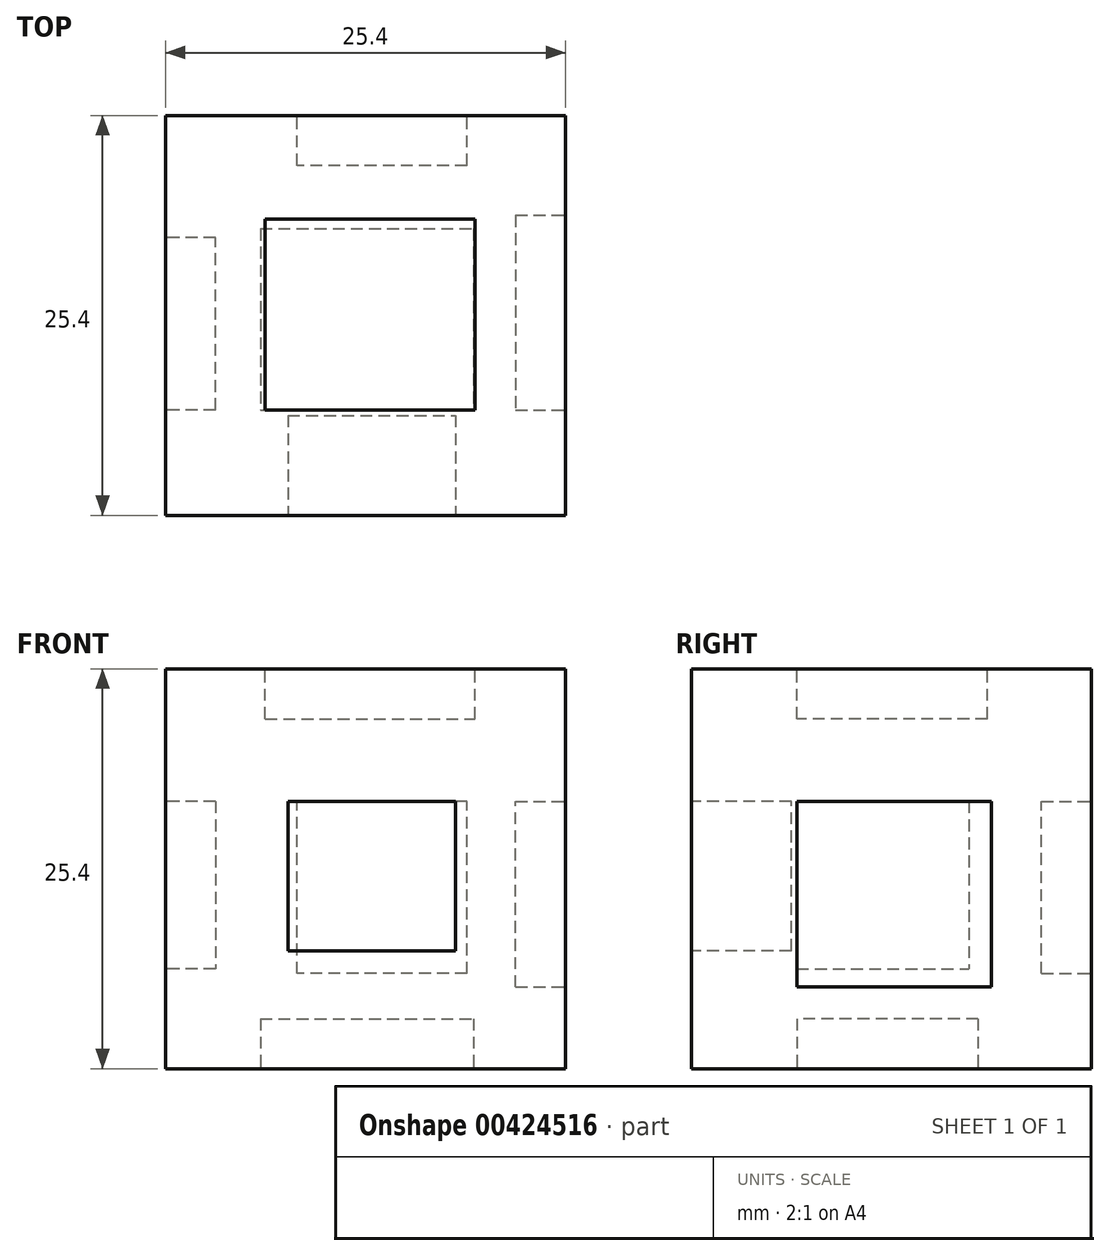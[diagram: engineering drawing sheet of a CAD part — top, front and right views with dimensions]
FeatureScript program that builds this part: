
annotation { "Feature Type Name" : "Feature", "Feature Type Description" : "" }
export const myFeature = defineFeature(function(context is Context, id is Id, definition is map)
    precondition{}
    {
        {
            var Q0;
            Q0=qCreatedBy(makeId("Right.planeOp"),FACE);
            var sketch = newSketch(context, id + "F0", { "sketchPlane" : qUnion([Q0])});
            skLineSegment(sketch, "E0.bottom", {"start": v(-6.7, 8.42) * mm, "end": v(18.7, 8.42) * mm});
            skLineSegment(sketch, "E0.top", {"start": v(-6.7, -16.98) * mm, "end": v(18.7, -16.98) * mm});
            skLineSegment(sketch, "E0.left", {"start": v(-6.7, 8.42) * mm, "end": v(-6.7, -16.98) * mm});
            skLineSegment(sketch, "E0.right", {"start": v(18.7, 8.42) * mm, "end": v(18.7, -16.98) * mm});
            skSolve(sketch);
        }
        {
            var Q0;
            Q0 = qSketchRegion(id + "F0", true);
            extrude(context, id + "F1", {"entities" : qUnion([Q0]), "depth" : 25.4 * mm});
        }
        {
            var Q0;
            Q0=makeQuery(id+"F1.opExtrude","SWEPT_FACE",FACE,{"disambiguationData":[OSD([sQuery(id+"F0.wireOp",EDGE,"E0.left")])]});
            var sketch = newSketch(context, id + "F2", { "sketchPlane" : qUnion([Q0])});
            skLineSegment(sketch, "E1.bottom", {"start": v(7.77, -9.5) * mm, "end": v(18.42, -9.5) * mm});
            skLineSegment(sketch, "E1.top", {"start": v(7.77, 0) * mm, "end": v(18.42, 0) * mm});
            skLineSegment(sketch, "E1.left", {"start": v(7.77, -9.5) * mm, "end": v(7.77, 0) * mm});
            skLineSegment(sketch, "E1.right", {"start": v(18.42, -9.5) * mm, "end": v(18.42, 0) * mm});
            skSolve(sketch);
        }
        {
            var Q0;
            Q0 = qSketchRegion(id + "F2", true);
            extrude(context, id + "F3", {"entities" : qUnion([Q0]), "oppositeDirection" : true, "depth" : 6.35 * mm});
        }
        {
            var Q0;
            Q0=makeQuery(id+"F1.opExtrude","CAP_FACE",FACE,{"disambiguationData":[OSD([sQuery(id+"F0.wireOp",EDGE,"E0.bottom"),sQuery(id+"F0.wireOp",EDGE,"E0.top"),sQuery(id+"F0.wireOp",EDGE,"E0.left"),sQuery(id+"F0.wireOp",EDGE,"E0.right")])],"isStart":true});
            var sketch = newSketch(context, id + "F4", { "sketchPlane" : qUnion([Q0])});
            skLineSegment(sketch, "E2.bottom", {"start": v(0, 0) * mm, "end": v(-10.94, 0) * mm});
            skLineSegment(sketch, "E2.top", {"start": v(0, -10.65) * mm, "end": v(-10.94, -10.65) * mm});
            skLineSegment(sketch, "E2.left", {"start": v(0, 0) * mm, "end": v(0, -10.65) * mm});
            skLineSegment(sketch, "E2.right", {"start": v(-10.94, 0) * mm, "end": v(-10.94, -10.65) * mm});
            skSolve(sketch);
        }
        {
            var Q0;
            Q0=makeQuery(id+"F1.opExtrude","CAP_FACE",FACE,{"disambiguationData":[OSD([sQuery(id+"F0.wireOp",EDGE,"E0.bottom"),sQuery(id+"F0.wireOp",EDGE,"E0.top"),sQuery(id+"F0.wireOp",EDGE,"E0.left"),sQuery(id+"F0.wireOp",EDGE,"E0.right")])],"isStart":false});
            var sketch = newSketch(context, id + "F5", { "sketchPlane" : qUnion([Q0])});
            skLineSegment(sketch, "E3.bottom", {"start": v(12.38, -11.8) * mm, "end": v(0, -11.8) * mm});
            skLineSegment(sketch, "E3.top", {"start": v(12.38, 0) * mm, "end": v(0, 0) * mm});
            skLineSegment(sketch, "E3.left", {"start": v(12.38, -11.8) * mm, "end": v(12.38, 0) * mm});
            skLineSegment(sketch, "E3.right", {"start": v(0, -11.8) * mm, "end": v(0, 0) * mm});
            skSolve(sketch);
        }
        {
            var Q0;
            Q0 = qSketchRegion(id + "F5", true);
            extrude(context, id + "F6", {"entities" : qUnion([Q0]), "oppositeDirection" : true, "depth" : 3.17 * mm});
        }
        {
            var Q0;
            Q0=makeQuery(id+"F1.opExtrude","SWEPT_FACE",FACE,{"disambiguationData":[OSD([sQuery(id+"F0.wireOp",EDGE,"E0.right")])]});
            var sketch = newSketch(context, id + "F7", { "sketchPlane" : qUnion([Q0])});
            skLineSegment(sketch, "E4.bottom", {"start": v(-19.15, -10.94) * mm, "end": v(-8.35, -10.94) * mm});
            skLineSegment(sketch, "E4.top", {"start": v(-19.15, 0) * mm, "end": v(-8.35, 0) * mm});
            skLineSegment(sketch, "E4.left", {"start": v(-19.15, -10.94) * mm, "end": v(-19.15, 0) * mm});
            skLineSegment(sketch, "E4.right", {"start": v(-8.35, -10.94) * mm, "end": v(-8.35, 0) * mm});
            skSolve(sketch);
        }
        {
            var Q0;
            Q0 = qSketchRegion(id + "F7", true);
            extrude(context, id + "F8", {"entities" : qUnion([Q0]), "oppositeDirection" : true, "depth" : 3.17 * mm});
        }
        {
            var Q0;
            Q0 = qSketchRegion(id + "F4", true);
            extrude(context, id + "F9", {"entities" : qUnion([Q0]), "oppositeDirection" : true, "depth" : 3.17 * mm});
        }
        {
            var Q0;
            Q0=makeQuery(id+"F1.opExtrude","SWEPT_FACE",FACE,{"disambiguationData":[OSD([sQuery(id+"F0.wireOp",EDGE,"E0.top")])]});
            var sketch = newSketch(context, id + "F10", { "sketchPlane" : qUnion([Q0])});
            skLineSegment(sketch, "E5.bottom", {"start": v(6.02, -11.51) * mm, "end": v(19.55, -11.51) * mm});
            skLineSegment(sketch, "E5.top", {"start": v(6.02, 0) * mm, "end": v(19.55, 0) * mm});
            skLineSegment(sketch, "E5.left", {"start": v(6.02, -11.51) * mm, "end": v(6.02, 0) * mm});
            skLineSegment(sketch, "E5.right", {"start": v(19.55, -11.51) * mm, "end": v(19.55, 0) * mm});
            skSolve(sketch);
        }
        {
            var Q0;
            Q0 = qSketchRegion(id + "F10", true);
            extrude(context, id + "F11", {"entities" : qUnion([Q0]), "oppositeDirection" : true, "depth" : 3.17 * mm});
        }
        {
            var Q0;
            Q0=makeQuery(id+"F1.opExtrude","SWEPT_FACE",FACE,{"disambiguationData":[OSD([sQuery(id+"F0.wireOp",EDGE,"E0.bottom")])]});
            var sketch = newSketch(context, id + "F12", { "sketchPlane" : qUnion([Q0])});
            skLineSegment(sketch, "E6.bottom", {"start": v(6.33, 12.1) * mm, "end": v(19.64, 12.1) * mm});
            skLineSegment(sketch, "E6.top", {"start": v(6.33, 0) * mm, "end": v(19.64, 0) * mm});
            skLineSegment(sketch, "E6.left", {"start": v(6.33, 12.1) * mm, "end": v(6.33, 0) * mm});
            skLineSegment(sketch, "E6.right", {"start": v(19.64, 12.1) * mm, "end": v(19.64, 0) * mm});
            skSolve(sketch);
        }
        {
            var Q0;
            Q0 = qSketchRegion(id + "F12", true);
            extrude(context, id + "F13", {"entities" : qUnion([Q0]), "oppositeDirection" : true, "depth" : 3.17 * mm});
        }
    });
